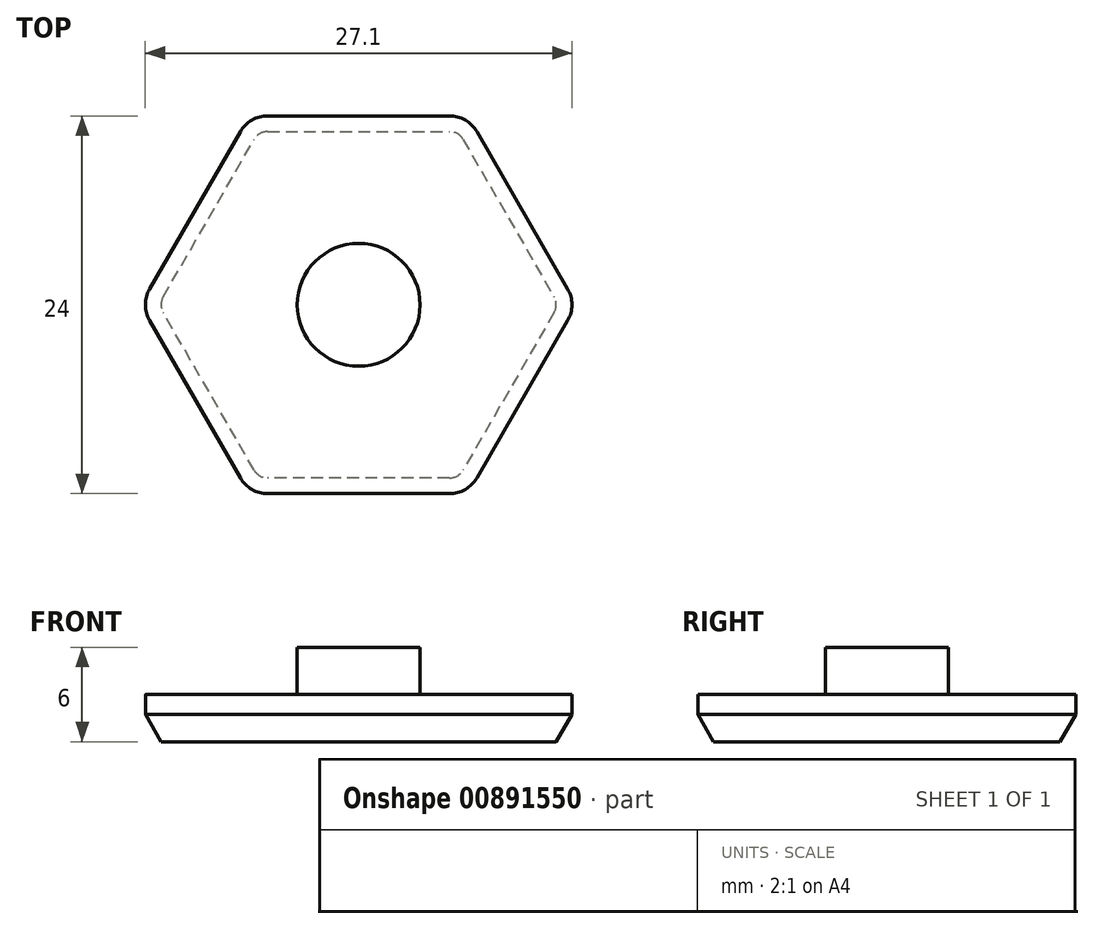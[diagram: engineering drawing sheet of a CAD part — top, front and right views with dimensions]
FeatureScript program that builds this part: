
annotation { "Feature Type Name" : "Feature", "Feature Type Description" : "" }
export const myFeature = defineFeature(function(context is Context, id is Id, definition is map)
    precondition{}
    {
        {
            var Q0;
            Q0=qCreatedBy(makeId("Top.planeOp"),FACE);
            var sketch = newSketch(context, id + "F0", { "sketchPlane" : qUnion([Q0])});
            skCircle(sketch, "E0", {"center": v(0, 0) * mm, "radius": 3.9 * mm});
            skSolve(sketch);
        }
        {
            var Q0;
            Q0=makeQuery(id+"F0.imprint","IMPRINT",FACE,{"disambiguationData":[TD([[makeQuery(id+"F0.imprint","IMPRINT",EDGE,{"derivedFrom":sQuery(id+"F0.wireOp",EDGE,"E0")}),1.0]])]});
            var sketch = newSketch(context, id + "F1", { "sketchPlane" : qUnion([Q0])});
            skCircle(sketch, "E1.cCircle", {"center": v(0, 0) * mm, "radius": 12 * mm, "construction": true});
            skLineSegment(sketch, "E1.0", {"start": v(6.93, -12) * mm, "end": v(-6.93, -12) * mm});
            skLineSegment(sketch, "E1.1", {"start": v(-6.93, -12) * mm, "end": v(-13.86, 0) * mm});
            skLineSegment(sketch, "E1.2", {"start": v(-13.86, 0) * mm, "end": v(-6.93, 12) * mm});
            skLineSegment(sketch, "E1.3", {"start": v(-6.93, 12) * mm, "end": v(6.93, 12) * mm});
            skLineSegment(sketch, "E1.4", {"start": v(6.93, 12) * mm, "end": v(13.86, 0) * mm});
            skLineSegment(sketch, "E1.5", {"start": v(13.86, 0) * mm, "end": v(6.93, -12) * mm});
            skPoint(sketch, "E1.0.midPoint", {"position": v(0, -12) * mm});
            skPoint(sketch, "E2.0.midPoint", {"position": v(0, -27.78) * mm});
            skSolve(sketch);
        }
        {
            var Q0;
            Q0=makeQuery(id+"F1.imprint","IMPRINT",FACE,{"disambiguationData":[TD([[makeQuery(id+"F1.imprint","IMPRINT",EDGE,{"derivedFrom":sQuery(id+"F1.wireOp",EDGE,"E1.0")}),-1.0]])]});
            extrude(context, id + "F2", {"entities" : qUnion([Q0]), "depth" : 3 * mm, "offsetDistance" : 25 * mm});
        }
        {
            var Q0;
            Q0=qCreatedBy(makeId("Top.planeOp"),FACE);
            var sketch = newSketch(context, id + "F3", { "sketchPlane" : qUnion([Q0])});
            skCircle(sketch, "E3", {"center": v(0, 0) * mm, "radius": 3.9 * mm});
            skSolve(sketch);
        }
        {
            var Q0;
            Q0 = qSketchRegion(id + "F3", true);
            extrude(context, id + "F4", {"entities" : qUnion([Q0]), "operationType" : NewBodyOperationType.ADD, "depth" : 6 * mm, "offsetDistance" : 25 * mm});
        }
        {
            var Q0;
            Q0=makeQuery(id+"F2.opExtrude","SWEPT_EDGE",EDGE,{"disambiguationData":[OSD([sQuery(id+"F1.wireOp",EDGE,"E1.4"),sQuery(id+"F1.wireOp",EDGE,"E1.5")])]});
            var Q1;
            Q1=makeQuery(id+"F2.opExtrude","SWEPT_EDGE",EDGE,{"disambiguationData":[OSD([sQuery(id+"F1.wireOp",EDGE,"E1.0"),sQuery(id+"F1.wireOp",EDGE,"E1.5")])]});
            var Q2;
            Q2=makeQuery(id+"F2.opExtrude","SWEPT_EDGE",EDGE,{"disambiguationData":[OSD([sQuery(id+"F1.wireOp",EDGE,"E1.0"),sQuery(id+"F1.wireOp",EDGE,"E1.1")])]});
            var Q3;
            Q3=makeQuery(id+"F2.opExtrude","SWEPT_EDGE",EDGE,{"disambiguationData":[OSD([sQuery(id+"F1.wireOp",EDGE,"E1.1"),sQuery(id+"F1.wireOp",EDGE,"E1.2")])]});
            var Q4;
            Q4=makeQuery(id+"F2.opExtrude","SWEPT_EDGE",EDGE,{"disambiguationData":[OSD([sQuery(id+"F1.wireOp",EDGE,"E1.2"),sQuery(id+"F1.wireOp",EDGE,"E1.3")])]});
            var Q5;
            Q5=makeQuery(id+"F2.opExtrude","SWEPT_EDGE",EDGE,{"disambiguationData":[OSD([sQuery(id+"F1.wireOp",EDGE,"E1.3"),sQuery(id+"F1.wireOp",EDGE,"E1.4")])]});
            fillet(context, id + "F5", {"entities" : qUnion([Q0, Q1, Q2, Q3, Q4, Q5]), "radius" : 2 * mm, "tangentPropagation" : true, "allowEdgeOverflow" : false});
        }
        {
            var Q0;
            Q0=makeQuery(id+"F2.opExtrude","CAP_EDGE",EDGE,{"disambiguationData":[OSD([sQuery(id+"F1.wireOp",EDGE,"E1.0")])],"isStart":true});
            chamfer(context, id + "F6", {"entities" : qUnion([Q0]), "chamferType" : ChamferType.OFFSET_ANGLE, "width" : 1 * mm, "oppositeDirection" : false, "angle" : 60 * degree, "tangentPropagation" : true});
        }
    });
